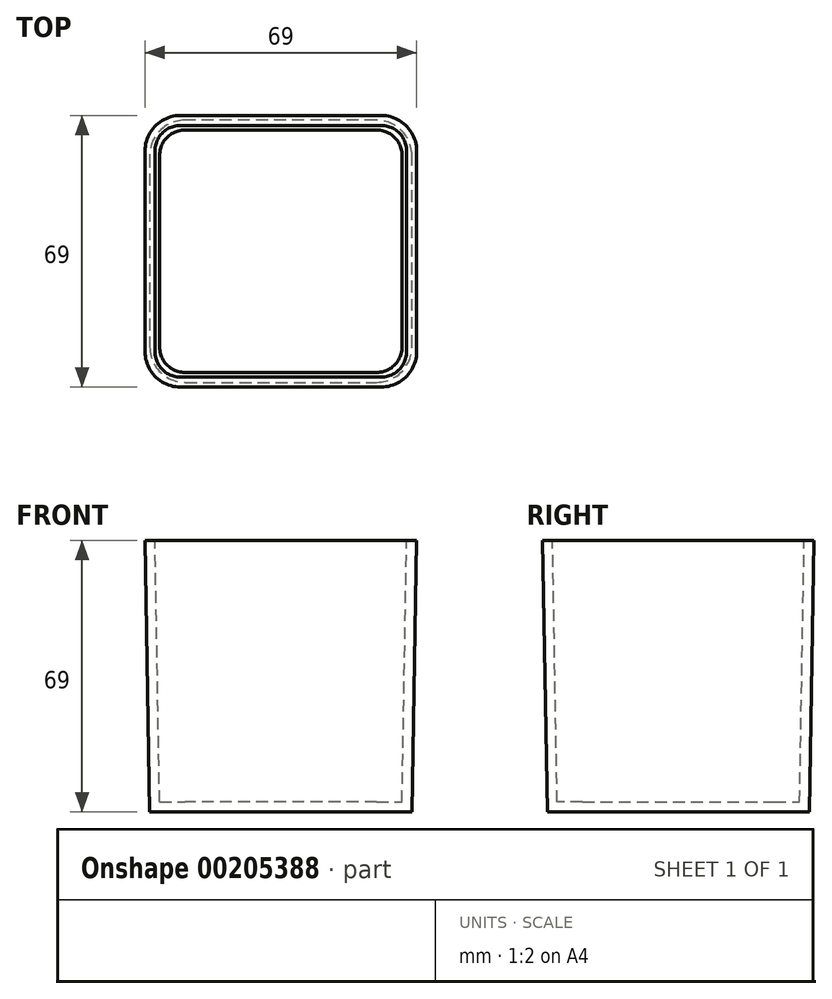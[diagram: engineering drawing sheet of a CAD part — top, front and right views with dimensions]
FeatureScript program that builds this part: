
annotation { "Feature Type Name" : "Feature", "Feature Type Description" : "" }
export const myFeature = defineFeature(function(context is Context, id is Id, definition is map)
    precondition{}
    {
        {
            var Q0;
            Q0=qCreatedBy(makeId("Top.planeOp"),FACE);
            var sketch = newSketch(context, id + "F0", { "sketchPlane" : qUnion([Q0])});
            skLineSegment(sketch, "E0.bottom", {"start": v(34.5, 34.5) * mm, "end": v(-34.5, 34.5) * mm});
            skLineSegment(sketch, "E0.top", {"start": v(34.5, -34.5) * mm, "end": v(-34.5, -34.5) * mm});
            skLineSegment(sketch, "E0.left", {"start": v(34.5, 34.5) * mm, "end": v(34.5, -34.5) * mm});
            skLineSegment(sketch, "E0.right", {"start": v(-34.5, 34.5) * mm, "end": v(-34.5, -34.5) * mm});
            skPoint(sketch, "E0.middle", {"position": v(0, 0) * mm});
            skSolve(sketch);
        }
        {
            var Q0;
            Q0 = qSketchRegion(id + "F0", true);
            extrude(context, id + "F1", {"entities" : qUnion([Q0]), "oppositeDirection" : true, "depth" : 69 * mm, "hasDraft" : true, "draftAngle" : 1 * degree, "draftPullDirection" : true});
        }
        {
            var Q0;
            Q0=makeQuery(id+"F1.opExtrude","SWEPT_EDGE",EDGE,{"disambiguationData":[OSD([sQuery(id+"F0.wireOp",EDGE,"E0.top"),sQuery(id+"F0.wireOp",EDGE,"E0.left")])]});
            var Q1;
            Q1=makeQuery(id+"F1.opExtrude","SWEPT_EDGE",EDGE,{"disambiguationData":[OSD([sQuery(id+"F0.wireOp",EDGE,"E0.bottom"),sQuery(id+"F0.wireOp",EDGE,"E0.left")])]});
            var Q2;
            Q2=makeQuery(id+"F1.opExtrude","SWEPT_EDGE",EDGE,{"disambiguationData":[OSD([sQuery(id+"F0.wireOp",EDGE,"E0.top"),sQuery(id+"F0.wireOp",EDGE,"E0.right")])]});
            var Q3;
            Q3=makeQuery(id+"F1.opExtrude","SWEPT_EDGE",EDGE,{"disambiguationData":[OSD([sQuery(id+"F0.wireOp",EDGE,"E0.bottom"),sQuery(id+"F0.wireOp",EDGE,"E0.right")])]});
            fillet(context, id + "F2", {"entities" : qUnion([Q0, Q1, Q2, Q3]), "radius" : 9 * mm, "tangentPropagation" : true, "allowEdgeOverflow" : false});
        }
        {
            var Q0;
            Q0=makeQuery(id+"F1.opExtrude","CAP_FACE",FACE,{"disambiguationData":[OSD([sQuery(id+"F0.wireOp",EDGE,"E0.bottom"),sQuery(id+"F0.wireOp",EDGE,"E0.top"),sQuery(id+"F0.wireOp",EDGE,"E0.left"),sQuery(id+"F0.wireOp",EDGE,"E0.right")])],"isStart":true});
            shell(context, id + "F3", {"entities" : qUnion([Q0]), "thickness" : 2.54 * mm});
        }
    });
